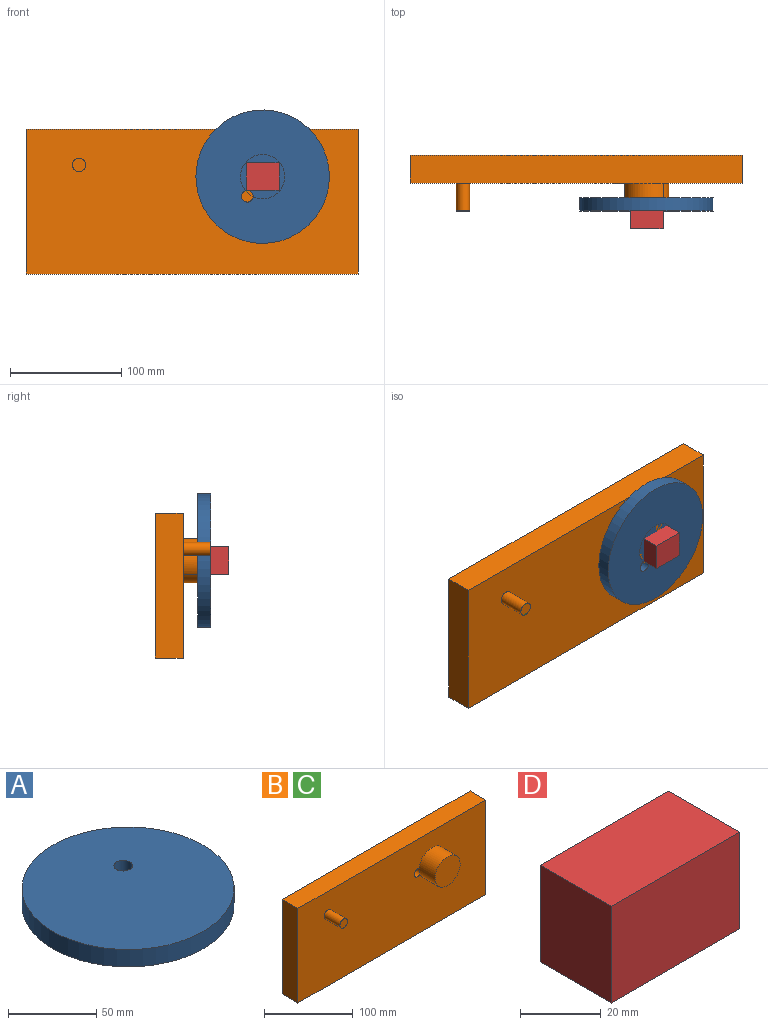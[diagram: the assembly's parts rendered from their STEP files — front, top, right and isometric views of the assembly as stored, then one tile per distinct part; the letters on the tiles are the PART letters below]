
ASSEMBLY  parts=4 mates=2
PART A: 4 faces, bbox 120x120x12 mm
  f0: cylinder r=60mm len=120mm, axis (0,0,-1), area 4523.9mm2, adj f1,f2
  f1: plane 120x120mm, normal (0,0,1), area 11223.1mm2, adj f0,f3
  f2: plane 120x120mm, normal (0,0,-1), area 11223.1mm2, adj f0,f3
  f3: cylinder r=5.25mm len=12mm, axis (0,0,1), area 395.8mm2, adj f1,f2
PART B: 12 faces, bbox 298.7x50x130 mm
  f0: plane 298.66x130mm, normal (0,-1,0), area 37391mm2, adj f1,f2,f3,f4,f6,f8,f9
  f1: plane 298.66x25mm, normal (0,0,1), area 7466.4mm2, adj f0,f2,f4,f5
  f2: plane 130x25mm, normal (-1,0,0), area 3250mm2, adj f0,f1,f3,f5
  f3: plane 298.66x25mm, normal (0,0,-1), area 7466.4mm2, adj f0,f2,f4,f5
  f4: plane 130x25mm, normal (1,0,0), area 3250mm2, adj f0,f1,f3,f5
  f5: plane 298.66x130mm, normal (0,1,0), area 38738.9mm2, adj f1,f2,f3,f4,f8
  f6: cylinder r=6mm len=25mm, axis (0,1,0), area 942.5mm2, adj f0,f7
  f7: plane 12x12mm, normal (0,-1,0), area 113.1mm2, adj f6
  f8: cylinder r=5.25mm len=25mm, axis (0,1,0), area 824.7mm2, adj f0,f5,f11
  f9: cylinder r=19.93mm len=39.86mm, axis (0,1,0), area 3130.3mm2, adj f0,f10,f11
  f10: plane 39.86x39.86mm, normal (0,-1,0), area 1247.6mm2, adj f9
  f11: plane 7.98x2.59mm, normal (0,1,0), area 12.9mm2, adj f8,f9
PART C: same geometry as B
PART D: 6 faces, bbox 45.1x25x29.4 mm
  f0: plane 45.1x25mm, normal (0,0,1), area 1127.6mm2, adj f1,f3,f4,f5
  f1: plane 29.36x25mm, normal (-1,0,0), area 733.9mm2, adj f0,f2,f4,f5
  f2: plane 45.1x25mm, normal (0,0,-1), area 1127.6mm2, adj f1,f3,f4,f5
  f3: plane 29.36x25mm, normal (1,0,0), area 733.9mm2, adj f0,f2,f4,f5
  f4: plane 45.1x29.36mm, normal (0,-1,0), area 1324.1mm2, adj f0,f1,f2,f3
  f5: plane 45.1x29.36mm, normal (0,1,0), area 1324.1mm2, adj f0,f1,f2,f3
PLACE A rot(axis=(0,-0.71,0.71),180deg) t=(-295.35,56.72,-2.18)mm
PLACE B t=(-226.29,29.72,-70.88)mm
PLACE C t=(-226.29,29.72,-70.88)mm
PLACE D rot(axis=(-0.58,0.58,-0.58),120deg) t=(-185.95,-189.58,-110.68)mm
MATE slider A.f1 <-> D.f3  axis (0,-1,0) through (-162.64,-20.28,-48.18)mm
MATE parallel A.f0 <-> C.f9  axis (0,-1,0) through (-162.74,-20.28,-48.31)mm
